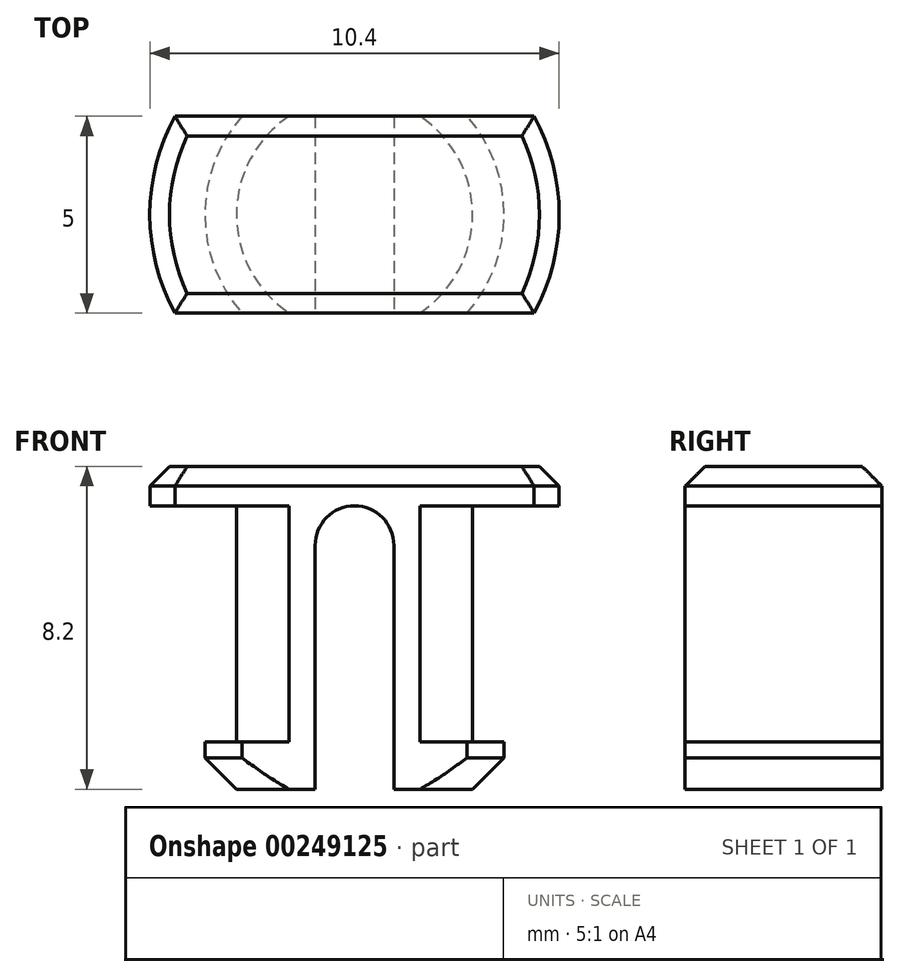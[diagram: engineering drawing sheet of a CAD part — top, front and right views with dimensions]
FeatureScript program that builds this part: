
annotation { "Feature Type Name" : "Feature", "Feature Type Description" : "" }
export const myFeature = defineFeature(function(context is Context, id is Id, definition is map)
    precondition{}
    {
        {
            var Q0;
            Q0=qCreatedBy(makeId("Front.planeOp"),FACE);
            var sketch = newSketch(context, id + "F0", { "sketchPlane" : qUnion([Q0])});
            skLineSegment(sketch, "E0", {"start": v(0, 8.2) * mm, "end": v(-5.2, 8.2) * mm});
            skLineSegment(sketch, "E1", {"start": v(-5.2, 8.2) * mm, "end": v(-5.2, 7.2) * mm});
            skLineSegment(sketch, "E2", {"start": v(-5.2, 7.2) * mm, "end": v(-3, 7.2) * mm});
            skLineSegment(sketch, "E3", {"start": v(-3, 7.2) * mm, "end": v(-3, 1.2) * mm});
            skLineSegment(sketch, "E4", {"start": v(-3, 1.2) * mm, "end": v(-3.8, 1.2) * mm});
            skLineSegment(sketch, "E5", {"start": v(-3.8, 1.2) * mm, "end": v(-3.8, 0) * mm});
            skLineSegment(sketch, "E6", {"start": v(-3.8, 0) * mm, "end": v(0, 0) * mm});
            skLineSegment(sketch, "E7", {"start": v(0, 0) * mm, "end": v(0, 8.2) * mm});
            skSolve(sketch);
        }
        {
            var Q0;
            Q0=makeQuery(id+"F0.imprint","IMPRINT",FACE,{"disambiguationData":[TD([[makeQuery(id+"F0.imprint","IMPRINT",EDGE,{"derivedFrom":sQuery(id+"F0.wireOp",EDGE,"E0")}),1.0]])]});
            var Q1;
            Q1=sQuery(id+"F0.wireOp",EDGE,"E7");
            revolve(context, id + "F1", {"entities" : qUnion([Q0]), "axis" : qUnion([Q1]), "revolveType" : RevolveType.FULL});
        }
        {
            var Q0;
            Q0=qCreatedBy(makeId("Top.planeOp"),FACE);
            var sketch = newSketch(context, id + "F2", { "sketchPlane" : qUnion([Q0])});
            skLineSegment(sketch, "E8.bottom", {"start": v(-14.4, 11.6) * mm, "end": v(18.38, 11.6) * mm});
            skLineSegment(sketch, "E8.top", {"start": v(-14.4, 2.5) * mm, "end": v(18.38, 2.5) * mm});
            skLineSegment(sketch, "E8.left", {"start": v(-14.4, 11.6) * mm, "end": v(-14.4, 2.5) * mm});
            skLineSegment(sketch, "E8.right", {"start": v(18.38, 11.6) * mm, "end": v(18.38, 2.5) * mm});
            skLineSegment(sketch, "E9.bottom", {"start": v(-8.5, -6.02) * mm, "end": v(12.41, -6.02) * mm});
            skLineSegment(sketch, "E9.top", {"start": v(-8.5, -2.5) * mm, "end": v(12.41, -2.5) * mm});
            skLineSegment(sketch, "E9.left", {"start": v(-8.5, -6.02) * mm, "end": v(-8.5, -2.5) * mm});
            skLineSegment(sketch, "E9.right", {"start": v(12.41, -6.02) * mm, "end": v(12.41, -2.5) * mm});
            skSolve(sketch);
        }
        {
            var Q0;
            Q0=makeQuery(id+"F2.imprint","IMPRINT",FACE,{"disambiguationData":[TD([[makeQuery(id+"F2.imprint","IMPRINT",EDGE,{"derivedFrom":sQuery(id+"F2.wireOp",EDGE,"E8.bottom")}),-1.0]])]});
            var Q1;
            Q1=makeQuery(id+"F2.imprint","IMPRINT",FACE,{"disambiguationData":[TD([[makeQuery(id+"F2.imprint","IMPRINT",EDGE,{"derivedFrom":sQuery(id+"F2.wireOp",EDGE,"E9.bottom")}),1.0]])]});
            extrude(context, id + "F3", {"entities" : qUnion([Q0, Q1]), "operationType" : NewBodyOperationType.REMOVE, "depth" : 25 * mm});
        }
        {
            var Q0;
            Q0=qCreatedBy(makeId("Front.planeOp"),FACE);
            var sketch = newSketch(context, id + "F4", { "sketchPlane" : qUnion([Q0])});
            skLineSegment(sketch, "E10.bottom", {"start": v(-1, 0) * mm, "end": v(1, 0) * mm});
            skLineSegment(sketch, "E10.top", {"start": v(-1, 7.2) * mm, "end": v(1, 7.2) * mm});
            skLineSegment(sketch, "E10.left", {"start": v(-1, 0) * mm, "end": v(-1, 7.2) * mm});
            skLineSegment(sketch, "E10.right", {"start": v(1, 0) * mm, "end": v(1, 7.2) * mm});
            skSolve(sketch);
        }
        {
            var Q0;
            Q0 = qSketchRegion(id + "F4", true);
            extrude(context, id + "F5", {"entities" : qUnion([Q0]), "operationType" : NewBodyOperationType.REMOVE, "oppositeDirection" : true, "depth" : 25 * mm, "hasSecondDirection" : true, "secondDirectionOppositeDirection" : false, "secondDirectionDepth" : 25 * mm});
        }
        {
            var Q0;
            Q0=makeQuery(id+"F5.boolean.opBoolean","COPY",EDGE,{"derivedFrom":makeQuery(id+"F5.opExtrude","SWEPT_EDGE",EDGE,{"disambiguationData":[OSD([sQuery(id+"F4.wireOp",EDGE,"E10.top"),sQuery(id+"F4.wireOp",EDGE,"E10.left")])]})});
            var Q1;
            Q1=makeQuery(id+"F5.boolean.opBoolean","COPY",EDGE,{"derivedFrom":makeQuery(id+"F5.opExtrude","SWEPT_EDGE",EDGE,{"disambiguationData":[OSD([sQuery(id+"F4.wireOp",EDGE,"E10.top"),sQuery(id+"F4.wireOp",EDGE,"E10.right")])]})});
            fillet(context, id + "F6", {"entities" : qUnion([Q0, Q1]), "radius" : 1 * mm, "tangentPropagation" : true, "allowEdgeOverflow" : false});
        }
        {
            var Q0;
            Q0=makeQuery(id+"F3.boolean.opBoolean","SPLIT",EDGE,{"disambiguationData":[OD(0.0)],"derivedFrom":makeQuery(id+"F1.opRevolve","SWEPT_EDGE",EDGE,{"disambiguationData":[OSD([sQuery(id+"F0.wireOp",EDGE,"E5"),sQuery(id+"F0.wireOp",EDGE,"E6")])]})});
            var Q1;
            Q1=makeQuery(id+"F3.boolean.opBoolean","SPLIT",EDGE,{"disambiguationData":[OD(1.0)],"derivedFrom":makeQuery(id+"F1.opRevolve","SWEPT_EDGE",EDGE,{"disambiguationData":[OSD([sQuery(id+"F0.wireOp",EDGE,"E5"),sQuery(id+"F0.wireOp",EDGE,"E6")])]})});
            chamfer(context, id + "F7", {"entities" : qUnion([Q0, Q1]), "width" : 0.8 * mm, "tangentPropagation" : true});
        }
        {
            var Q0;
            Q0=makeQuery(id+"F1.opRevolve","SWEPT_FACE",FACE,{"disambiguationData":[OSD([sQuery(id+"F0.wireOp",EDGE,"E0")])]});
            chamfer(context, id + "F8", {"entities" : qUnion([Q0]), "width" : .5 * mm, "tangentPropagation" : true});
        }
    });
